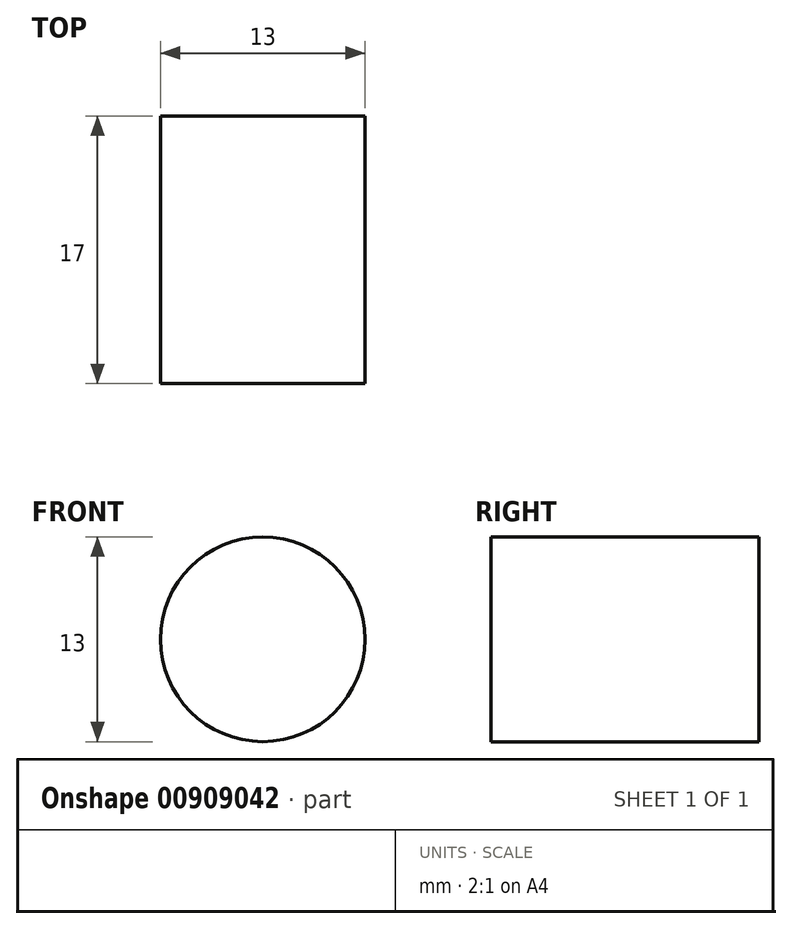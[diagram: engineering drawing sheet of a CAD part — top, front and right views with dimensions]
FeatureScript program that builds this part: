
annotation { "Feature Type Name" : "Feature", "Feature Type Description" : "" }
export const myFeature = defineFeature(function(context is Context, id is Id, definition is map)
    precondition{}
    {
        {
            var Q0;
            Q0=qCreatedBy(makeId("Front.planeOp"),FACE);
            var sketch = newSketch(context, id + "F0", { "sketchPlane" : qUnion([Q0])});
            skCircle(sketch, "E0", {"center": v(0, 0) * mm, "radius": 6.5 * mm});
            skSolve(sketch);
        }
        {
            var Q0;
            Q0=makeQuery(id+"F0.imprint","IMPRINT",FACE,{"disambiguationData":[TD([[makeQuery(id+"F0.imprint","IMPRINT",EDGE,{"derivedFrom":sQuery(id+"F0.wireOp",EDGE,"E0")}),1.0]])]});
            extrude(context, id + "F1", {"entities" : qUnion([Q0]), "depth" : 17 * mm, "offsetDistance" : 25 * mm});
        }
    });
